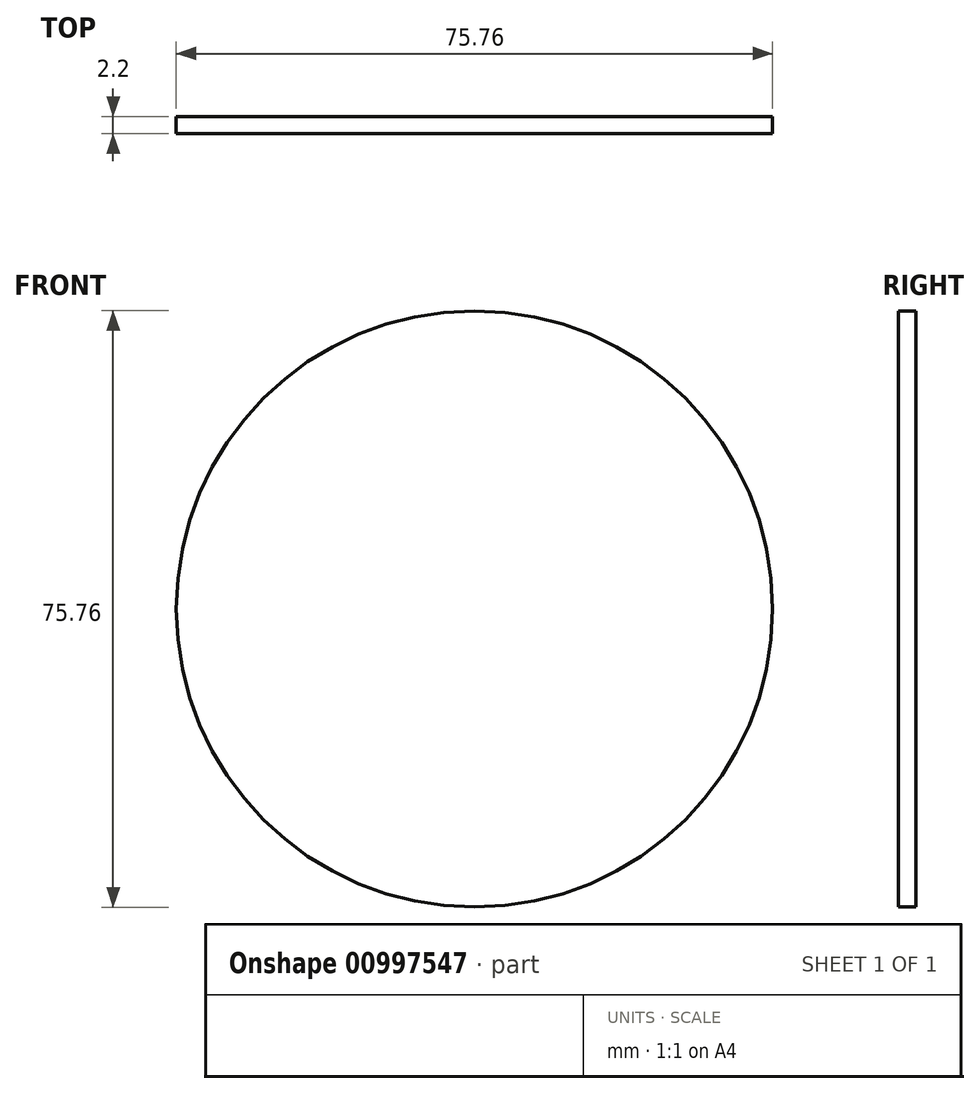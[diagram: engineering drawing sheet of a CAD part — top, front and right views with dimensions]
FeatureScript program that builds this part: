
annotation { "Feature Type Name" : "Feature", "Feature Type Description" : "" }
export const myFeature = defineFeature(function(context is Context, id is Id, definition is map)
    precondition{}
    {
        {
            var Q0;
            Q0=qCreatedBy(makeId("Front.planeOp"),FACE);
            var sketch = newSketch(context, id + "F0", { "sketchPlane" : qUnion([Q0])});
            skCircle(sketch, "E0", {"center": v(0, 0) * mm, "radius": 37.88 * mm});
            skSolve(sketch);
        }
        {
            var Q0;
            Q0=makeQuery(id+"F0.imprint","IMPRINT",FACE,{"disambiguationData":[TD([[makeQuery(id+"F0.imprint","IMPRINT",EDGE,{"derivedFrom":sQuery(id+"F0.wireOp",EDGE,"E0")}),1.0]])]});
            extrude(context, id + "F1", {"entities" : qUnion([Q0]), "endBound" : BoundingType.SYMMETRIC, "depth" : 2.2 * mm, "offsetDistance" : 25 * mm});
        }
    });
